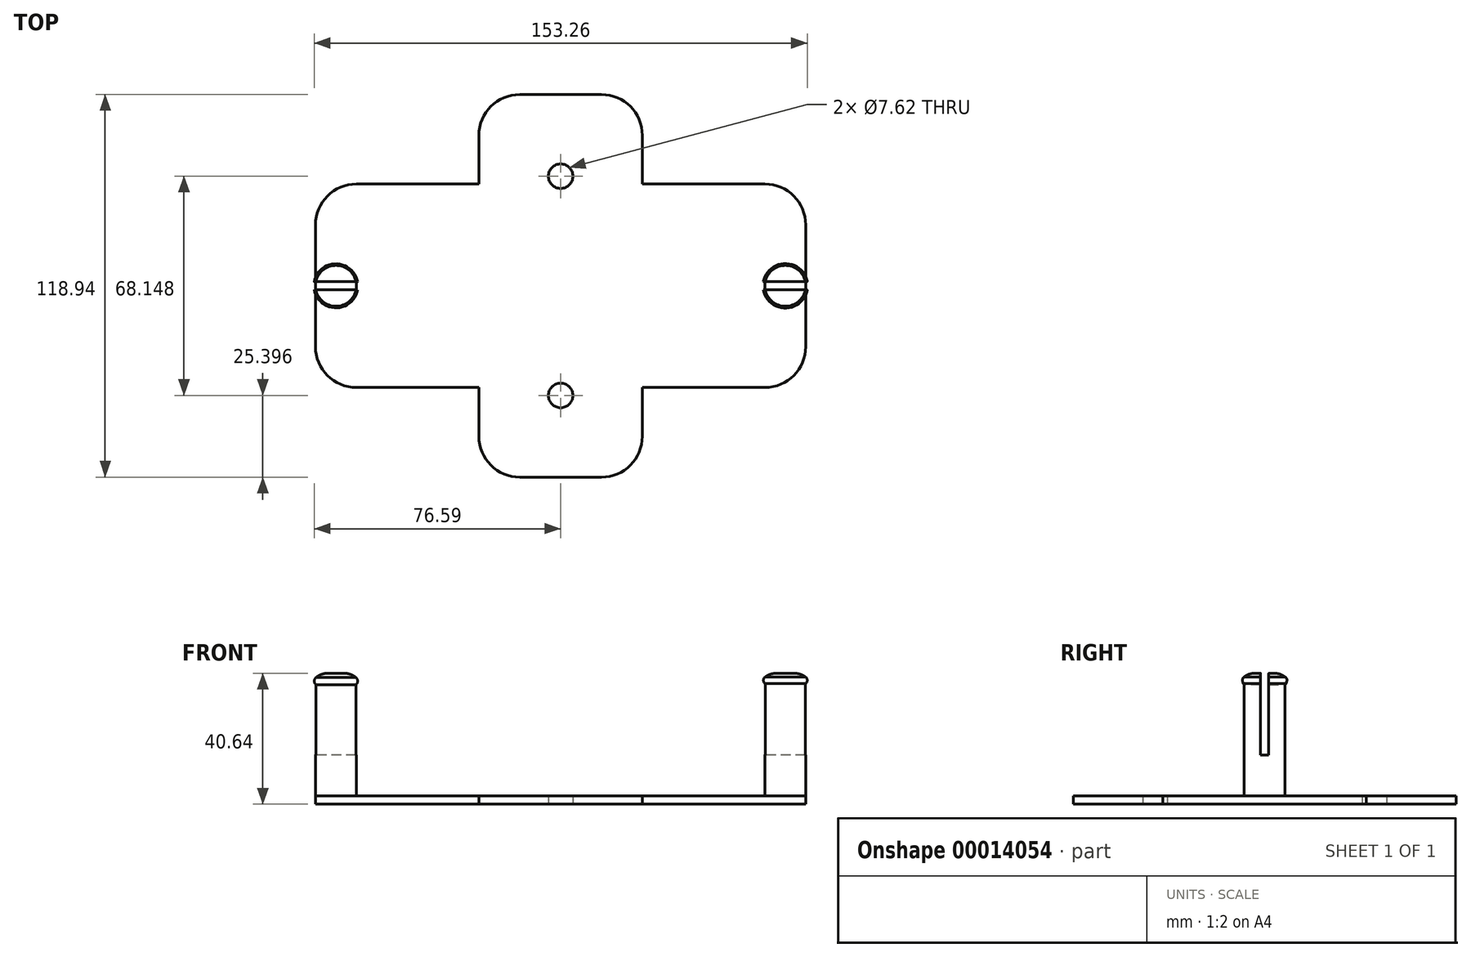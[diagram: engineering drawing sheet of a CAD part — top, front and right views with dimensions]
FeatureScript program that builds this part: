
annotation { "Feature Type Name" : "Feature", "Feature Type Description" : "" }
export const myFeature = defineFeature(function(context is Context, id is Id, definition is map)
    precondition{}
    {
        {
            var Q0;
            Q0=qCreatedBy(makeId("Top.planeOp"),FACE);
            var sketch = newSketch(context, id + "F0", { "sketchPlane" : qUnion([Q0])});
            skPoint(sketch, "E0.rect.middle", {"position": v(0, 0) * mm});
            skCircle(sketch, "E1", {"center": v(0, 34.07) * mm, "radius": 3.81 * mm});
            skCircle(sketch, "E2", {"center": v(0, -34.07) * mm, "radius": 3.81 * mm});
            skLineSegment(sketch, "E3.top", {"start": v(76.2, 31.61) * mm, "end": v(25.4, 31.61) * mm});
            skLineSegment(sketch, "E3.right", {"start": v(25.4, 59.47) * mm, "end": v(25.4, 31.61) * mm});
            skLineSegment(sketch, "E4.0.MirrorCS", {"start": v(-25.4, 59.47) * mm, "end": v(-25.4, 31.61) * mm});
            skLineSegment(sketch, "E5.0.MirrorCS", {"start": v(-76.2, 31.61) * mm, "end": v(-25.4, 31.61) * mm});
            skLineSegment(sketch, "E6.0.MirrorCS", {"start": v(76.2, -31.61) * mm, "end": v(25.4, -31.61) * mm});
            skLineSegment(sketch, "E7.0.MirrorCS", {"start": v(25.4, -59.47) * mm, "end": v(25.4, -31.61) * mm});
            skLineSegment(sketch, "E8.0.MirrorCS", {"start": v(-76.2, -31.61) * mm, "end": v(-25.4, -31.61) * mm});
            skLineSegment(sketch, "E9.0.MirrorCS", {"start": v(-25.4, -59.47) * mm, "end": v(-25.4, -31.61) * mm});
            skLineSegment(sketch, "E10", {"start": v(-25.4, 59.47) * mm, "end": v(25.4, 59.47) * mm});
            skLineSegment(sketch, "E11", {"start": v(76.2, 31.61) * mm, "end": v(76.2, -31.61) * mm});
            skLineSegment(sketch, "E12", {"start": v(25.4, -59.47) * mm, "end": v(-25.4, -59.47) * mm});
            skLineSegment(sketch, "E13", {"start": v(-76.2, -31.61) * mm, "end": v(-76.2, 31.61) * mm});
            skSolve(sketch);
        }
        {
            var Q0;
            Q0=makeQuery(id+"F0.imprint","IMPRINT",FACE,{"disambiguationData":[TD([[makeQuery(id+"F0.imprint","IMPRINT",EDGE,{"derivedFrom":sQuery(id+"F0.wireOp",EDGE,"E1")}),-1.0]])]});
            extrude(context, id + "F1", {"entities" : qUnion([Q0]), "depth" : 2.54 * mm});
        }
        {
            var Q0;
            Q0=makeQuery(id+"F1.opExtrude","CAP_FACE",FACE,{"disambiguationData":[OSD([sQuery(id+"F0.wireOp",EDGE,"E1"),sQuery(id+"F0.wireOp",EDGE,"E2"),sQuery(id+"F0.wireOp",EDGE,"E3.top"),sQuery(id+"F0.wireOp",EDGE,"E3.right"),sQuery(id+"F0.wireOp",EDGE,"E4.0.MirrorCS"),sQuery(id+"F0.wireOp",EDGE,"E5.0.MirrorCS"),sQuery(id+"F0.wireOp",EDGE,"E6.0.MirrorCS"),sQuery(id+"F0.wireOp",EDGE,"E7.0.MirrorCS"),sQuery(id+"F0.wireOp",EDGE,"E8.0.MirrorCS"),sQuery(id+"F0.wireOp",EDGE,"E9.0.MirrorCS"),sQuery(id+"F0.wireOp",EDGE,"E10"),sQuery(id+"F0.wireOp",EDGE,"E11"),sQuery(id+"F0.wireOp",EDGE,"E12"),sQuery(id+"F0.wireOp",EDGE,"E13")])],"isStart":false});
            var sketch = newSketch(context, id + "F2", { "sketchPlane" : qUnion([Q0])});
            skCircle(sketch, "E14", {"center": v(69.85, 0) * mm, "radius": 6.35 * mm});
            skCircle(sketch, "E15", {"center": v(-69.85, 0) * mm, "radius": 6.35 * mm});
            skSolve(sketch);
        }
        {
            var Q0;
            Q0 = qSketchRegion(id + "F2", true);
            extrude(context, id + "F3", {"entities" : qUnion([Q0]), "operationType" : NewBodyOperationType.ADD, "depth" : 38.1 * mm});
        }
        {
            var Q0;
            Q0=qCreatedBy(makeId("Front.planeOp"),FACE);
            var sketch = newSketch(context, id + "F4", { "sketchPlane" : qUnion([Q0])});
            skArc(sketch, "E16", {"start": v(63.5, 39.54) * mm, "mid": v(62.91, 38.48) * mm, "end": v(63.5, 37.41) * mm});
            skLineSegment(sketch, "E17", {"start": v(63.5, 39.54) * mm, "end": v(63.5, 37.41) * mm});
            skSolve(sketch);
        }
        {
            var Q0;
            Q0=makeQuery(id+"F4.imprint","IMPRINT",FACE,{"disambiguationData":[TD([[makeQuery(id+"F4.imprint","IMPRINT",EDGE,{"derivedFrom":sQuery(id+"F4.wireOp",EDGE,"E16")}),1.0]])]});
            var Q1;
            Q1=makeQuery(id+"F3.opExtrude","CAP_EDGE",EDGE,{"disambiguationData":[OSD([sQuery(id+"F2.wireOp",EDGE,"E14")])],"isStart":false});
            sweep(context, id + "F5", {"operationType" : NewBodyOperationType.ADD, "profiles" : qUnion([Q0]), "path" : qUnion([Q1])});
        }
        {
            var Q0;
            Q0=makeQuery(id+"F3.opExtrude","CAP_EDGE",EDGE,{"disambiguationData":[OSD([sQuery(id+"F2.wireOp",EDGE,"E14")])],"isStart":false});
            fillet(context, id + "F6", {"entities" : qUnion([Q0]), "radius" : 5.08 * mm, "tangentPropagation" : true, "allowEdgeOverflow" : false});
        }
        {
            var Q0;
            Q0=qCreatedBy(makeId("Front.planeOp"),FACE);
            var sketch = newSketch(context, id + "F7", { "sketchPlane" : qUnion([Q0])});
            skArc(sketch, "E18", {"start": v(-63.57, 37.03) * mm, "mid": v(-63, 38.2) * mm, "end": v(-63.58, 39.37) * mm});
            skLineSegment(sketch, "E19", {"start": v(-63.58, 39.37) * mm, "end": v(-63.57, 37.03) * mm});
            skSolve(sketch);
        }
        {
            var Q0;
            Q0=makeQuery(id+"F7.imprint","IMPRINT",FACE,{"disambiguationData":[TD([[makeQuery(id+"F7.imprint","IMPRINT",EDGE,{"derivedFrom":sQuery(id+"F7.wireOp",EDGE,"E18")}),1.0]])]});
            var Q1;
            Q1=makeQuery(id+"F3.opExtrude","CAP_EDGE",EDGE,{"disambiguationData":[OSD([sQuery(id+"F2.wireOp",EDGE,"E15")])],"isStart":false});
            sweep(context, id + "F8", {"operationType" : NewBodyOperationType.ADD, "profiles" : qUnion([Q0]), "path" : qUnion([Q1])});
        }
        {
            var Q0;
            Q0=makeQuery(id+"F3.opExtrude","CAP_EDGE",EDGE,{"disambiguationData":[OSD([sQuery(id+"F2.wireOp",EDGE,"E15")])],"isStart":false});
            fillet(context, id + "F9", {"entities" : qUnion([Q0]), "radius" : 5.08 * mm, "tangentPropagation" : true, "allowEdgeOverflow" : false});
        }
        {
            var Q0;
            Q0=makeQuery(id+"F1.opExtrude","SWEPT_EDGE",EDGE,{"disambiguationData":[OSD([sQuery(id+"F0.wireOp",EDGE,"E6.0.MirrorCS"),sQuery(id+"F0.wireOp",EDGE,"E11")])]});
            var Q1;
            Q1=makeQuery(id+"F1.opExtrude","SWEPT_EDGE",EDGE,{"disambiguationData":[OSD([sQuery(id+"F0.wireOp",EDGE,"E3.top"),sQuery(id+"F0.wireOp",EDGE,"E11")])]});
            var Q2;
            Q2=makeQuery(id+"F1.opExtrude","SWEPT_EDGE",EDGE,{"disambiguationData":[OSD([sQuery(id+"F0.wireOp",EDGE,"E5.0.MirrorCS"),sQuery(id+"F0.wireOp",EDGE,"E13")])]});
            var Q3;
            Q3=makeQuery(id+"F1.opExtrude","SWEPT_EDGE",EDGE,{"disambiguationData":[OSD([sQuery(id+"F0.wireOp",EDGE,"E8.0.MirrorCS"),sQuery(id+"F0.wireOp",EDGE,"E13")])]});
            var Q4;
            Q4=makeQuery(id+"F1.opExtrude","SWEPT_EDGE",EDGE,{"disambiguationData":[OSD([sQuery(id+"F0.wireOp",EDGE,"E9.0.MirrorCS"),sQuery(id+"F0.wireOp",EDGE,"E12")])]});
            var Q5;
            Q5=makeQuery(id+"F1.opExtrude","SWEPT_EDGE",EDGE,{"disambiguationData":[OSD([sQuery(id+"F0.wireOp",EDGE,"E7.0.MirrorCS"),sQuery(id+"F0.wireOp",EDGE,"E12")])]});
            var Q6;
            Q6=makeQuery(id+"F1.opExtrude","SWEPT_EDGE",EDGE,{"disambiguationData":[OSD([sQuery(id+"F0.wireOp",EDGE,"E3.right"),sQuery(id+"F0.wireOp",EDGE,"E10")])]});
            var Q7;
            Q7=makeQuery(id+"F1.opExtrude","SWEPT_EDGE",EDGE,{"disambiguationData":[OSD([sQuery(id+"F0.wireOp",EDGE,"E4.0.MirrorCS"),sQuery(id+"F0.wireOp",EDGE,"E10")])]});
            fillet(context, id + "F10", {"entities" : qUnion([Q0, Q1, Q2, Q3, Q4, Q5, Q6, Q7]), "radius" : 12.7 * mm, "tangentPropagation" : true, "allowEdgeOverflow" : false});
        }
        {
            var Q0;
            Q0=makeQuery(id+"F3.opExtrude","CAP_FACE",FACE,{"disambiguationData":[OSD([sQuery(id+"F2.wireOp",EDGE,"E14")])],"isStart":false});
            var sketch = newSketch(context, id + "F11", { "sketchPlane" : qUnion([Q0])});
            skLineSegment(sketch, "E20.rect.bottom", {"start": v(77.48, 1.27) * mm, "end": v(62.22, 1.27) * mm});
            skLineSegment(sketch, "E20.rect.top", {"start": v(77.48, -1.27) * mm, "end": v(62.22, -1.27) * mm});
            skLineSegment(sketch, "E20.rect.left", {"start": v(77.48, 1.27) * mm, "end": v(77.48, -1.27) * mm});
            skLineSegment(sketch, "E20.rect.right", {"start": v(62.22, 1.27) * mm, "end": v(62.22, -1.27) * mm});
            skPoint(sketch, "E20.rect.middle", {"position": v(69.85, 0) * mm});
            skSolve(sketch);
        }
        {
            var Q0;
            Q0 = qSketchRegion(id + "F11", true);
            extrude(context, id + "F12", {"entities" : qUnion([Q0]), "operationType" : NewBodyOperationType.REMOVE, "oppositeDirection" : true, "depth" : 25.4 * mm});
        }
        {
            var Q0;
            Q0=makeQuery(id+"F3.opExtrude","CAP_FACE",FACE,{"disambiguationData":[OSD([sQuery(id+"F2.wireOp",EDGE,"E15")])],"isStart":false});
            var sketch = newSketch(context, id + "F13", { "sketchPlane" : qUnion([Q0])});
            skLineSegment(sketch, "E21.rect.bottom", {"start": v(-62.58, 1.27) * mm, "end": v(-77.12, 1.27) * mm});
            skLineSegment(sketch, "E21.rect.top", {"start": v(-62.58, -1.27) * mm, "end": v(-77.12, -1.27) * mm});
            skLineSegment(sketch, "E21.rect.left", {"start": v(-62.58, 1.27) * mm, "end": v(-62.58, -1.27) * mm});
            skLineSegment(sketch, "E21.rect.right", {"start": v(-77.12, 1.27) * mm, "end": v(-77.12, -1.27) * mm});
            skPoint(sketch, "E21.rect.middle", {"position": v(-69.85, 0) * mm});
            skSolve(sketch);
        }
        {
            var Q0;
            Q0 = qSketchRegion(id + "F13", true);
            extrude(context, id + "F14", {"entities" : qUnion([Q0]), "operationType" : NewBodyOperationType.REMOVE, "oppositeDirection" : true, "depth" : 25.4 * mm});
        }
    });
